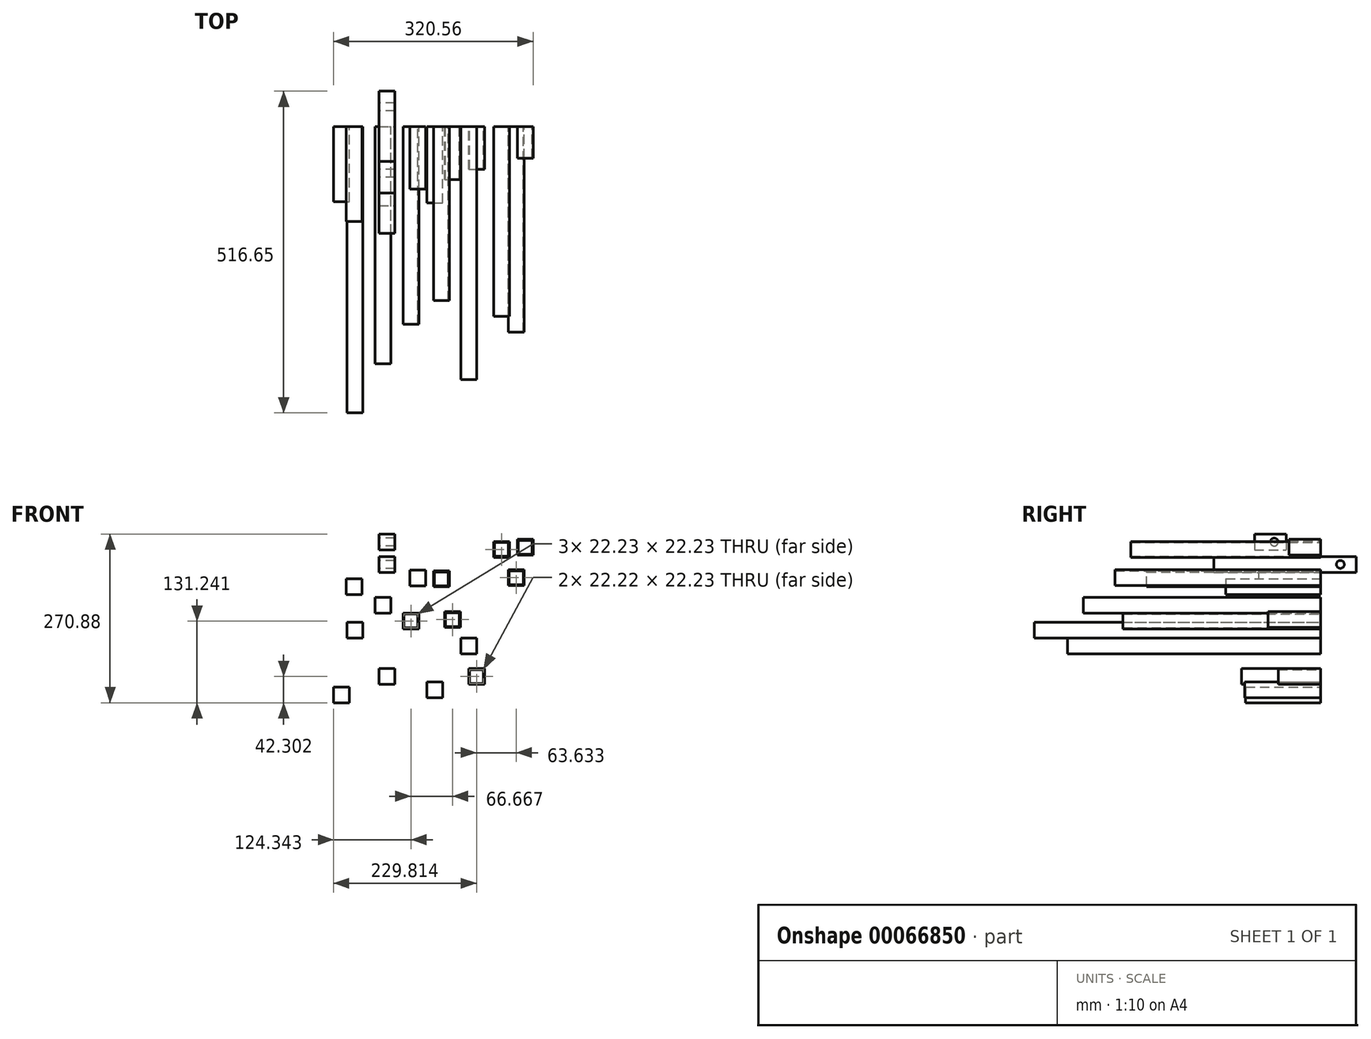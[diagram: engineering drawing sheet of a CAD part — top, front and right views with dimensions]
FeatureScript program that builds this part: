
annotation { "Feature Type Name" : "Feature", "Feature Type Description" : "" }
export const myFeature = defineFeature(function(context is Context, id is Id, definition is map)
    precondition{}
    {
        {
            var Q0;
            Q0=qCreatedBy(makeId("Front.planeOp"),FACE);
            var sketch = newSketch(context, id + "F0", { "sketchPlane" : qUnion([Q0])});
            skLineSegment(sketch, "E0.bottom", {"start": v(-6.69, -14.03) * mm, "end": v(18.71, -14.03) * mm});
            skLineSegment(sketch, "E0.top", {"start": v(-6.69, 11.37) * mm, "end": v(18.71, 11.37) * mm});
            skLineSegment(sketch, "E0.left", {"start": v(-6.69, -14.03) * mm, "end": v(-6.69, 11.37) * mm});
            skLineSegment(sketch, "E0.right", {"start": v(18.71, -14.03) * mm, "end": v(18.71, 11.37) * mm});
            skSolve(sketch);
        }
        {
            var Q0;
            Q0=makeQuery(id+"F0.imprint","IMPRINT",FACE,{"disambiguationData":[TD([[makeQuery(id+"F0.imprint","IMPRINT",EDGE,{"derivedFrom":sQuery(id+"F0.wireOp",EDGE,"E0.bottom")}),1.0]])]});
            extrude(context, id + "F1", {"entities" : qUnion([Q0]), "depth" : 381 * mm});
        }
        {
            var Q0;
            Q0=qCreatedBy(makeId("Front.planeOp"),FACE);
            var sketch = newSketch(context, id + "F2", { "sketchPlane" : qUnion([Q0])});
            skLineSegment(sketch, "E1.bottom", {"start": v(38.41, -39.74) * mm, "end": v(63.81, -39.74) * mm});
            skLineSegment(sketch, "E1.top", {"start": v(38.41, -14.34) * mm, "end": v(63.81, -14.34) * mm});
            skLineSegment(sketch, "E1.left", {"start": v(38.41, -39.74) * mm, "end": v(38.41, -14.34) * mm});
            skLineSegment(sketch, "E1.right", {"start": v(63.81, -39.74) * mm, "end": v(63.81, -14.34) * mm});
            skLineSegment(sketch, "E2.0", {"start": v(62.23, -38.15) * mm, "end": v(62.23, -15.93) * mm});
            skLineSegment(sketch, "E2.1", {"start": v(40, -38.15) * mm, "end": v(62.23, -38.15) * mm});
            skLineSegment(sketch, "E2.2", {"start": v(40, -38.15) * mm, "end": v(40, -15.93) * mm});
            skLineSegment(sketch, "E2.3", {"start": v(40, -15.93) * mm, "end": v(62.23, -15.93) * mm});
            skSolve(sketch);
        }
        {
            var Q0;
            Q0=makeQuery(id+"F2.imprint","IMPRINT",FACE,{"disambiguationData":[TD([[makeQuery(id+"F2.imprint","IMPRINT",EDGE,{"derivedFrom":sQuery(id+"F2.wireOp",EDGE,"E1.bottom")}),1.0]])]});
            extrude(context, id + "F3", {"entities" : qUnion([Q0]), "depth" : 317.5 * mm});
        }
        {
            var Q0;
            Q0=qCreatedBy(makeId("Front.planeOp"),FACE);
            var sketch = newSketch(context, id + "F4", { "sketchPlane" : qUnion([Q0])});
            skLineSegment(sketch, "E3.bottom", {"start": v(-52.82, 41.02) * mm, "end": v(-27.42, 41.02) * mm});
            skLineSegment(sketch, "E3.top", {"start": v(-52.82, 15.62) * mm, "end": v(-27.42, 15.62) * mm});
            skLineSegment(sketch, "E3.left", {"start": v(-52.82, 41.02) * mm, "end": v(-52.82, 15.62) * mm});
            skLineSegment(sketch, "E3.right", {"start": v(-27.42, 41.02) * mm, "end": v(-27.42, 15.62) * mm});
            skSolve(sketch);
        }
        {
            var Q0;
            Q0=makeQuery(id+"F4.imprint","IMPRINT",FACE,{"disambiguationData":[TD([[makeQuery(id+"F4.imprint","IMPRINT",EDGE,{"derivedFrom":sQuery(id+"F4.wireOp",EDGE,"E3.bottom")}),-1.0]])]});
            extrude(context, id + "F5", {"entities" : qUnion([Q0]), "depth" : 152.4 * mm});
        }
        {
            var Q0;
            Q0=qCreatedBy(makeId("Right.planeOp"),FACE);
            var sketch = newSketch(context, id + "F6", { "sketchPlane" : qUnion([Q0])});
            skLineSegment(sketch, "E4.bottom", {"start": v(-171.69, 76.74) * mm, "end": v(56.91, 76.74) * mm});
            skLineSegment(sketch, "E4.top", {"start": v(-171.69, 51.34) * mm, "end": v(56.91, 51.34) * mm});
            skLineSegment(sketch, "E4.left", {"start": v(-171.69, 76.74) * mm, "end": v(-171.69, 51.34) * mm});
            skLineSegment(sketch, "E4.right", {"start": v(56.91, 76.74) * mm, "end": v(56.91, 51.34) * mm});
            skCircle(sketch, "E5", {"center": v(31.51, 64.04) * mm, "radius": 6.35 * mm});
            skPoint(sketch, "E5.centerSnap0", {"position": v(56.91, 64.04) * mm});
            skSolve(sketch);
        }
        {
            var Q0;
            Q0=makeQuery(id+"F6.imprint","IMPRINT",FACE,{"disambiguationData":[TD([[makeQuery(id+"F6.imprint","IMPRINT",EDGE,{"derivedFrom":sQuery(id+"F6.wireOp",EDGE,"E4.bottom")}),-1.0]])]});
            extrude(context, id + "F7", {"entities" : qUnion([Q0]), "depth" : 25.4 * mm});
        }
        {
            var Q0;
            Q0=qCreatedBy(makeId("Right.planeOp"),FACE);
            var sketch = newSketch(context, id + "F8", { "sketchPlane" : qUnion([Q0])});
            skLineSegment(sketch, "E6.bottom", {"start": v(-106.42, 112.6) * mm, "end": v(-55.62, 112.6) * mm});
            skLineSegment(sketch, "E6.top", {"start": v(-106.42, 87.2) * mm, "end": v(-55.62, 87.2) * mm});
            skLineSegment(sketch, "E6.left", {"start": v(-106.42, 112.6) * mm, "end": v(-106.42, 87.2) * mm});
            skLineSegment(sketch, "E6.right", {"start": v(-55.62, 112.6) * mm, "end": v(-55.62, 87.2) * mm});
            skCircle(sketch, "E7", {"center": v(-74.67, 99.9) * mm, "radius": 6.35 * mm});
            skPoint(sketch, "E7.centerSnap0", {"position": v(-55.62, 99.9) * mm});
            skSolve(sketch);
        }
        {
            var Q0;
            Q0=makeQuery(id+"F8.imprint","IMPRINT",FACE,{"disambiguationData":[TD([[makeQuery(id+"F8.imprint","IMPRINT",EDGE,{"derivedFrom":sQuery(id+"F8.wireOp",EDGE,"E6.bottom")}),-1.0]])]});
            extrude(context, id + "F9", {"entities" : qUnion([Q0]), "depth" : 25.4 * mm});
        }
        {
            var Q0;
            Q0=qCreatedBy(makeId("Front.planeOp"),FACE);
            var sketch = newSketch(context, id + "F10", { "sketchPlane" : qUnion([Q0])});
            skLineSegment(sketch, "E8.bottom", {"start": v(-51.42, -54.05) * mm, "end": v(-26.02, -54.05) * mm});
            skLineSegment(sketch, "E8.top", {"start": v(-51.42, -28.65) * mm, "end": v(-26.02, -28.65) * mm});
            skLineSegment(sketch, "E8.left", {"start": v(-51.42, -54.05) * mm, "end": v(-51.42, -28.65) * mm});
            skLineSegment(sketch, "E8.right", {"start": v(-26.02, -54.05) * mm, "end": v(-26.02, -28.65) * mm});
            skSolve(sketch);
        }
        {
            var Q0;
            Q0=makeQuery(id+"F10.imprint","IMPRINT",FACE,{"disambiguationData":[TD([[makeQuery(id+"F10.imprint","IMPRINT",EDGE,{"derivedFrom":sQuery(id+"F10.wireOp",EDGE,"E8.bottom")}),1.0]])]});
            extrude(context, id + "F11", {"entities" : qUnion([Q0]), "depth" : 459.74 * mm});
        }
        {
            var Q0;
            Q0=qCreatedBy(makeId("Front.planeOp"),FACE);
            var sketch = newSketch(context, id + "F12", { "sketchPlane" : qUnion([Q0])});
            skLineSegment(sketch, "E9.bottom", {"start": v(49.68, 54.58) * mm, "end": v(75.08, 54.58) * mm});
            skLineSegment(sketch, "E9.top", {"start": v(49.68, 29.18) * mm, "end": v(75.08, 29.18) * mm});
            skLineSegment(sketch, "E9.left", {"start": v(49.68, 54.58) * mm, "end": v(49.68, 29.18) * mm});
            skLineSegment(sketch, "E9.right", {"start": v(75.08, 54.58) * mm, "end": v(75.08, 29.18) * mm});
            skSolve(sketch);
        }
        {
            var Q0;
            Q0=makeQuery(id+"F12.imprint","IMPRINT",FACE,{"disambiguationData":[TD([[makeQuery(id+"F12.imprint","IMPRINT",EDGE,{"derivedFrom":sQuery(id+"F12.wireOp",EDGE,"E9.bottom")}),-1.0]])]});
            extrude(context, id + "F13", {"entities" : qUnion([Q0]), "depth" : 100.08 * mm});
        }
        {
            var Q0;
            Q0=qCreatedBy(makeId("Front.planeOp"),FACE);
            var sketch = newSketch(context, id + "F14", { "sketchPlane" : qUnion([Q0])});
            skLineSegment(sketch, "E10.bottom", {"start": v(76.44, -124.58) * mm, "end": v(101.84, -124.58) * mm});
            skLineSegment(sketch, "E10.top", {"start": v(76.44, -149.98) * mm, "end": v(101.84, -149.98) * mm});
            skLineSegment(sketch, "E10.left", {"start": v(76.44, -124.58) * mm, "end": v(76.44, -149.98) * mm});
            skLineSegment(sketch, "E10.right", {"start": v(101.84, -124.58) * mm, "end": v(101.84, -149.98) * mm});
            skSolve(sketch);
        }
        {
            var Q0;
            Q0=makeQuery(id+"F14.imprint","IMPRINT",FACE,{"disambiguationData":[TD([[makeQuery(id+"F14.imprint","IMPRINT",EDGE,{"derivedFrom":sQuery(id+"F14.wireOp",EDGE,"E10.bottom")}),-1.0]])]});
            extrude(context, id + "F15", {"entities" : qUnion([Q0]), "depth" : 122.33 * mm});
        }
        {
            var Q0;
            Q0=qCreatedBy(makeId("Front.planeOp"),FACE);
            var sketch = newSketch(context, id + "F16", { "sketchPlane" : qUnion([Q0])});
            skLineSegment(sketch, "E11.bottom", {"start": v(-73.23, -132.88) * mm, "end": v(-47.83, -132.88) * mm});
            skLineSegment(sketch, "E11.top", {"start": v(-73.23, -158.28) * mm, "end": v(-47.83, -158.28) * mm});
            skLineSegment(sketch, "E11.left", {"start": v(-73.23, -132.88) * mm, "end": v(-73.23, -158.28) * mm});
            skLineSegment(sketch, "E11.right", {"start": v(-47.83, -132.88) * mm, "end": v(-47.83, -158.28) * mm});
            skSolve(sketch);
        }
        {
            var Q0;
            Q0=makeQuery(id+"F16.imprint","IMPRINT",FACE,{"disambiguationData":[TD([[makeQuery(id+"F16.imprint","IMPRINT",EDGE,{"derivedFrom":sQuery(id+"F16.wireOp",EDGE,"E11.bottom")}),-1.0]])]});
            extrude(context, id + "F17", {"entities" : qUnion([Q0]), "depth" : 120.6 * mm});
        }
        {
            var Q0;
            Q0=qCreatedBy(makeId("Front.planeOp"),FACE);
            var sketch = newSketch(context, id + "F18", { "sketchPlane" : qUnion([Q0])});
            skLineSegment(sketch, "E12.bottom", {"start": v(0, -103.28) * mm, "end": v(25.4, -103.28) * mm});
            skLineSegment(sketch, "E12.top", {"start": v(0, -128.68) * mm, "end": v(25.4, -128.68) * mm});
            skLineSegment(sketch, "E12.left", {"start": v(0, -103.28) * mm, "end": v(0, -128.68) * mm});
            skLineSegment(sketch, "E12.right", {"start": v(25.4, -103.28) * mm, "end": v(25.4, -128.68) * mm});
            skSolve(sketch);
        }
        {
            var Q0;
            Q0=makeQuery(id+"F18.imprint","IMPRINT",FACE,{"disambiguationData":[TD([[makeQuery(id+"F18.imprint","IMPRINT",EDGE,{"derivedFrom":sQuery(id+"F18.wireOp",EDGE,"E12.bottom")}),-1.0]])]});
            extrude(context, id + "F19", {"entities" : qUnion([Q0]), "depth" : 127 * mm});
        }
        {
            var Q0;
            Q0=qCreatedBy(makeId("Front.planeOp"),FACE);
            var sketch = newSketch(context, id + "F20", { "sketchPlane" : qUnion([Q0])});
            skLineSegment(sketch, "E13.bottom", {"start": v(131.36, -54.53) * mm, "end": v(156.76, -54.53) * mm});
            skLineSegment(sketch, "E13.top", {"start": v(131.36, -79.93) * mm, "end": v(156.76, -79.93) * mm});
            skLineSegment(sketch, "E13.left", {"start": v(131.36, -54.53) * mm, "end": v(131.36, -79.93) * mm});
            skLineSegment(sketch, "E13.right", {"start": v(156.76, -54.53) * mm, "end": v(156.76, -79.93) * mm});
            skSolve(sketch);
        }
        {
            var Q0;
            Q0=makeQuery(id+"F20.imprint","IMPRINT",FACE,{"disambiguationData":[TD([[makeQuery(id+"F20.imprint","IMPRINT",EDGE,{"derivedFrom":sQuery(id+"F20.wireOp",EDGE,"E13.bottom")}),-1.0]])]});
            extrude(context, id + "F21", {"entities" : qUnion([Q0]), "depth" : 406.4 * mm});
        }
        {
            var Q0;
            Q0=qCreatedBy(makeId("Front.planeOp"),FACE);
            var sketch = newSketch(context, id + "F22", { "sketchPlane" : qUnion([Q0])});
            skLineSegment(sketch, "E14.rect.bottom", {"start": v(111.05, 29.62) * mm, "end": v(88.82, 29.62) * mm});
            skLineSegment(sketch, "E14.rect.top", {"start": v(111.05, 51.84) * mm, "end": v(88.82, 51.84) * mm});
            skLineSegment(sketch, "E14.rect.left", {"start": v(111.05, 29.62) * mm, "end": v(111.05, 51.84) * mm});
            skLineSegment(sketch, "E14.rect.right", {"start": v(88.82, 29.62) * mm, "end": v(88.82, 51.84) * mm});
            skPoint(sketch, "E14.rect.middle", {"position": v(99.93, 40.73) * mm});
            skLineSegment(sketch, "E15.0", {"start": v(112.63, 53.43) * mm, "end": v(87.23, 53.43) * mm});
            skLineSegment(sketch, "E15.1", {"start": v(112.63, 28.03) * mm, "end": v(112.63, 53.43) * mm});
            skLineSegment(sketch, "E15.2", {"start": v(112.63, 28.03) * mm, "end": v(87.23, 28.03) * mm});
            skLineSegment(sketch, "E15.3", {"start": v(87.23, 28.03) * mm, "end": v(87.23, 53.43) * mm});
            skSolve(sketch);
        }
        {
            var Q0;
            Q0 = qSketchRegion(id + "F22", true);
            extrude(context, id + "F23", {"entities" : qUnion([Q0]), "depth" : 279.4 * mm});
        }
        {
            var Q0;
            Q0=qCreatedBy(makeId("Front.planeOp"),FACE);
            var sketch = newSketch(context, id + "F24", { "sketchPlane" : qUnion([Q0])});
            skLineSegment(sketch, "E16.bottom", {"start": v(183.84, 75.25) * mm, "end": v(209.24, 75.25) * mm});
            skLineSegment(sketch, "E16.top", {"start": v(183.84, 100.65) * mm, "end": v(209.24, 100.65) * mm});
            skLineSegment(sketch, "E16.left", {"start": v(183.84, 75.25) * mm, "end": v(183.84, 100.65) * mm});
            skLineSegment(sketch, "E16.right", {"start": v(209.24, 75.25) * mm, "end": v(209.24, 100.65) * mm});
            skLineSegment(sketch, "E17.bottom", {"start": v(185.43, 99.07) * mm, "end": v(207.66, 99.07) * mm});
            skLineSegment(sketch, "E17.top", {"start": v(185.43, 76.84) * mm, "end": v(207.66, 76.84) * mm});
            skLineSegment(sketch, "E17.left", {"start": v(185.43, 99.07) * mm, "end": v(185.43, 76.84) * mm});
            skLineSegment(sketch, "E17.right", {"start": v(207.66, 99.07) * mm, "end": v(207.66, 76.84) * mm});
            skSolve(sketch);
        }
        {
            var Q0;
            Q0=makeQuery(id+"F24.imprint","IMPRINT",FACE,{"disambiguationData":[TD([[makeQuery(id+"F24.imprint","IMPRINT",EDGE,{"derivedFrom":sQuery(id+"F24.wireOp",EDGE,"E16.bottom")}),1.0]])]});
            extrude(context, id + "F25", {"entities" : qUnion([Q0]), "depth" : 304.8 * mm});
        }
        {
            var Q0;
            Q0=qCreatedBy(makeId("Front.planeOp"),FACE);
            var sketch = newSketch(context, id + "F26", { "sketchPlane" : qUnion([Q0])});
            skLineSegment(sketch, "E18.bottom", {"start": v(221.93, 104.17) * mm, "end": v(247.33, 104.17) * mm});
            skLineSegment(sketch, "E18.top", {"start": v(221.93, 78.77) * mm, "end": v(247.33, 78.77) * mm});
            skLineSegment(sketch, "E18.left", {"start": v(221.93, 104.17) * mm, "end": v(221.93, 78.77) * mm});
            skLineSegment(sketch, "E18.right", {"start": v(247.33, 104.17) * mm, "end": v(247.33, 78.77) * mm});
            skLineSegment(sketch, "E19.bottom", {"start": v(223.52, 80.36) * mm, "end": v(245.74, 80.36) * mm});
            skLineSegment(sketch, "E19.top", {"start": v(223.52, 102.58) * mm, "end": v(245.74, 102.58) * mm});
            skLineSegment(sketch, "E19.left", {"start": v(223.52, 80.36) * mm, "end": v(223.52, 102.58) * mm});
            skLineSegment(sketch, "E19.right", {"start": v(245.74, 80.36) * mm, "end": v(245.74, 102.58) * mm});
            skSolve(sketch);
        }
        {
            var Q0;
            Q0=makeQuery(id+"F26.imprint","IMPRINT",FACE,{"disambiguationData":[TD([[makeQuery(id+"F26.imprint","IMPRINT",EDGE,{"derivedFrom":sQuery(id+"F26.wireOp",EDGE,"E18.bottom")}),-1.0]])]});
            extrude(context, id + "F27", {"entities" : qUnion([Q0]), "depth" : 50.8 * mm});
        }
        {
            var Q0;
            Q0=qCreatedBy(makeId("Front.planeOp"),FACE);
            var sketch = newSketch(context, id + "F28", { "sketchPlane" : qUnion([Q0])});
            skLineSegment(sketch, "E20.bottom", {"start": v(207.52, 55.28) * mm, "end": v(232.92, 55.28) * mm});
            skLineSegment(sketch, "E20.top", {"start": v(207.52, 29.88) * mm, "end": v(232.92, 29.88) * mm});
            skLineSegment(sketch, "E20.left", {"start": v(207.52, 55.28) * mm, "end": v(207.52, 29.88) * mm});
            skLineSegment(sketch, "E20.right", {"start": v(232.92, 55.28) * mm, "end": v(232.92, 29.88) * mm});
            skLineSegment(sketch, "E21.0", {"start": v(231.33, 53.7) * mm, "end": v(231.33, 31.47) * mm});
            skLineSegment(sketch, "E21.1", {"start": v(209.1, 53.7) * mm, "end": v(231.33, 53.7) * mm});
            skLineSegment(sketch, "E21.2", {"start": v(209.1, 53.7) * mm, "end": v(209.1, 31.47) * mm});
            skLineSegment(sketch, "E21.3", {"start": v(209.1, 31.47) * mm, "end": v(231.33, 31.47) * mm});
            skSolve(sketch);
        }
        {
            var Q0;
            Q0=makeQuery(id+"F28.imprint","IMPRINT",FACE,{"disambiguationData":[TD([[makeQuery(id+"F28.imprint","IMPRINT",EDGE,{"derivedFrom":sQuery(id+"F28.wireOp",EDGE,"E20.bottom")}),-1.0]])]});
            extrude(context, id + "F29", {"entities" : qUnion([Q0]), "depth" : 330.2 * mm});
        }
        {
            var Q0;
            Q0=qCreatedBy(makeId("Front.planeOp"),FACE);
            var sketch = newSketch(context, id + "F30", { "sketchPlane" : qUnion([Q0])});
            skLineSegment(sketch, "E22.bottom", {"start": v(105.08, -37.45) * mm, "end": v(130.48, -37.45) * mm});
            skLineSegment(sketch, "E22.top", {"start": v(105.08, -12.05) * mm, "end": v(130.48, -12.05) * mm});
            skLineSegment(sketch, "E22.left", {"start": v(105.08, -37.45) * mm, "end": v(105.08, -12.05) * mm});
            skLineSegment(sketch, "E22.right", {"start": v(130.48, -37.45) * mm, "end": v(130.48, -12.05) * mm});
            skLineSegment(sketch, "E23.0", {"start": v(128.9, -35.86) * mm, "end": v(128.9, -13.64) * mm});
            skLineSegment(sketch, "E23.1", {"start": v(106.67, -35.86) * mm, "end": v(128.9, -35.86) * mm});
            skLineSegment(sketch, "E23.2", {"start": v(106.67, -35.86) * mm, "end": v(106.67, -13.64) * mm});
            skLineSegment(sketch, "E23.3", {"start": v(106.67, -13.64) * mm, "end": v(128.9, -13.64) * mm});
            skSolve(sketch);
        }
        {
            var Q0;
            Q0=makeQuery(id+"F30.imprint","IMPRINT",FACE,{"disambiguationData":[TD([[makeQuery(id+"F30.imprint","IMPRINT",EDGE,{"derivedFrom":sQuery(id+"F30.wireOp",EDGE,"E22.bottom")}),1.0]])]});
            extrude(context, id + "F31", {"entities" : qUnion([Q0]), "depth" : 84.84 * mm});
        }
        {
            var Q0;
            Q0=qCreatedBy(makeId("Front.planeOp"),FACE);
            var sketch = newSketch(context, id + "F32", { "sketchPlane" : qUnion([Q0])});
            skLineSegment(sketch, "E24.bottom", {"start": v(143.88, -128.68) * mm, "end": v(169.28, -128.68) * mm});
            skLineSegment(sketch, "E24.top", {"start": v(143.88, -103.28) * mm, "end": v(169.28, -103.28) * mm});
            skLineSegment(sketch, "E24.left", {"start": v(143.88, -128.68) * mm, "end": v(143.88, -103.28) * mm});
            skLineSegment(sketch, "E24.right", {"start": v(169.28, -128.68) * mm, "end": v(169.28, -103.28) * mm});
            skLineSegment(sketch, "E25.0", {"start": v(167.7, -127.1) * mm, "end": v(167.7, -104.87) * mm});
            skLineSegment(sketch, "E25.1", {"start": v(145.47, -127.1) * mm, "end": v(167.7, -127.1) * mm});
            skLineSegment(sketch, "E25.2", {"start": v(145.47, -127.1) * mm, "end": v(145.47, -104.87) * mm});
            skLineSegment(sketch, "E25.3", {"start": v(145.47, -104.87) * mm, "end": v(167.7, -104.87) * mm});
            skSolve(sketch);
        }
        {
            var Q0;
            Q0=makeQuery(id+"F32.imprint","IMPRINT",FACE,{"disambiguationData":[TD([[makeQuery(id+"F32.imprint","IMPRINT",EDGE,{"derivedFrom":sQuery(id+"F32.wireOp",EDGE,"E24.bottom")}),1.0]])]});
            extrude(context, id + "F33", {"entities" : qUnion([Q0]), "depth" : 68.26 * mm});
        }
    });
